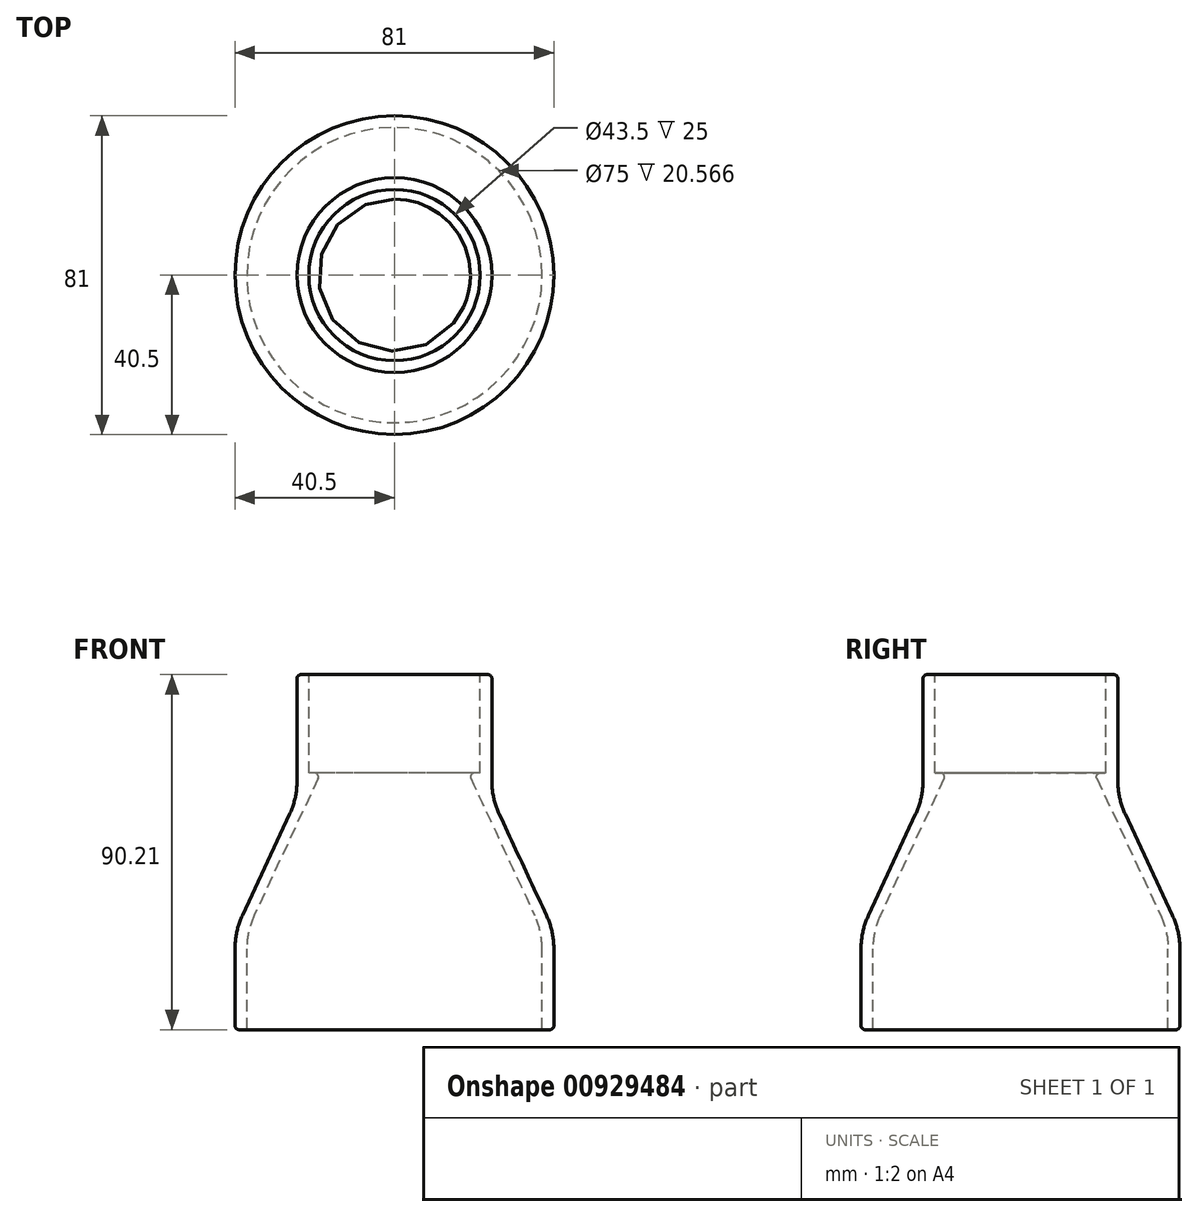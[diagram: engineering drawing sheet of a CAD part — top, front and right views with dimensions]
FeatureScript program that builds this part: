
annotation { "Feature Type Name" : "Feature", "Feature Type Description" : "" }
export const myFeature = defineFeature(function(context is Context, id is Id, definition is map)
    precondition{}
    {
        {
            var Q0;
            Q0=qCreatedBy(makeId("Front.planeOp"),FACE);
            var sketch = newSketch(context, id + "F0", { "sketchPlane" : qUnion([Q0])});
            skLineSegment(sketch, "E0", {"start": v(0, 86.32) * mm, "end": v(0, -61.46) * mm, "construction": true});
            skLineSegment(sketch, "E1", {"start": v(37.5, 0) * mm, "end": v(37.5, 20.57) * mm});
            skLineSegment(sketch, "E2", {"start": v(35.63, 29.02) * mm, "end": v(19.41, 63.79) * mm});
            skLineSegment(sketch, "E3", {"start": v(20.32, 65.2) * mm, "end": v(21.75, 65.2) * mm});
            skLineSegment(sketch, "E4", {"start": v(21.75, 65.2) * mm, "end": v(21.75, 90.2) * mm});
            skLineSegment(sketch, "E5", {"start": v(21.75, 90.2) * mm, "end": v(24.75, 90.2) * mm});
            skLineSegment(sketch, "E6", {"start": v(24.75, 90.2) * mm, "end": v(24.75, 63.2) * mm});
            skLineSegment(sketch, "E7", {"start": v(26.62, 54.76) * mm, "end": v(38.63, 29.02) * mm});
            skLineSegment(sketch, "E8", {"start": v(40.5, 20.57) * mm, "end": v(40.5, 0) * mm});
            skLineSegment(sketch, "E9", {"start": v(40.5, 0) * mm, "end": v(37.5, 0) * mm});
            skPoint(sketch, "E10.visualSharp", {"position": v(24.75, 58.78) * mm});
            skArc(sketch, "E10.filletArc", {"start": v(24.75, 63.2) * mm, "mid": v(25.22, 58.88) * mm, "end": v(26.62, 54.76) * mm});
            skPoint(sketch, "E11.visualSharp", {"position": v(40.5, 25) * mm});
            skArc(sketch, "E11.filletArc", {"start": v(40.5, 20.57) * mm, "mid": v(40.03, 24.9) * mm, "end": v(38.63, 29.02) * mm});
            skPoint(sketch, "E12.visualSharp", {"position": v(37.5, 25) * mm});
            skArc(sketch, "E12.filletArc", {"start": v(37.5, 20.57) * mm, "mid": v(37.03, 24.9) * mm, "end": v(35.63, 29.02) * mm});
            skPoint(sketch, "E13.visualSharp", {"position": v(18.75, 65.2) * mm});
            skArc(sketch, "E13.filletArc", {"start": v(20.32, 65.2) * mm, "mid": v(19.48, 64.75) * mm, "end": v(19.41, 63.79) * mm});
            skSolve(sketch);
        }
        {
            var Q0;
            Q0=makeQuery(id+"F0.imprint","IMPRINT",FACE,{"disambiguationData":[TD([[makeQuery(id+"F0.imprint","IMPRINT",EDGE,{"derivedFrom":sQuery(id+"F0.wireOp",EDGE,"E1")}),-1.0]])]});
            var Q1;
            Q1=sQuery(id+"F0.wireOp",EDGE,"E0");
            revolve(context, id + "F1", {"surfaceOperationType" : NewSurfaceOperationType.NEW, "entities" : qUnion([Q0]), "axis" : qUnion([Q1]), "revolveType" : RevolveType.FULL});
        }
        {
            var Q0;
            Q0=makeQuery(id+"F1.opRevolve","SWEPT_EDGE",EDGE,{"disambiguationData":[OSD([sQuery(id+"F0.wireOp",EDGE,"E8"),sQuery(id+"F0.wireOp",EDGE,"E9")])]});
            var Q1;
            Q1=makeQuery(id+"F1.opRevolve","SWEPT_EDGE",EDGE,{"disambiguationData":[OSD([sQuery(id+"F0.wireOp",EDGE,"E5"),sQuery(id+"F0.wireOp",EDGE,"E6")])]});
            fillet(context, id + "F2", {"entities" : qUnion([Q0, Q1]), "radius" : 1 * mm, "tangentPropagation" : true, "allowEdgeOverflow" : false});
        }
    });
